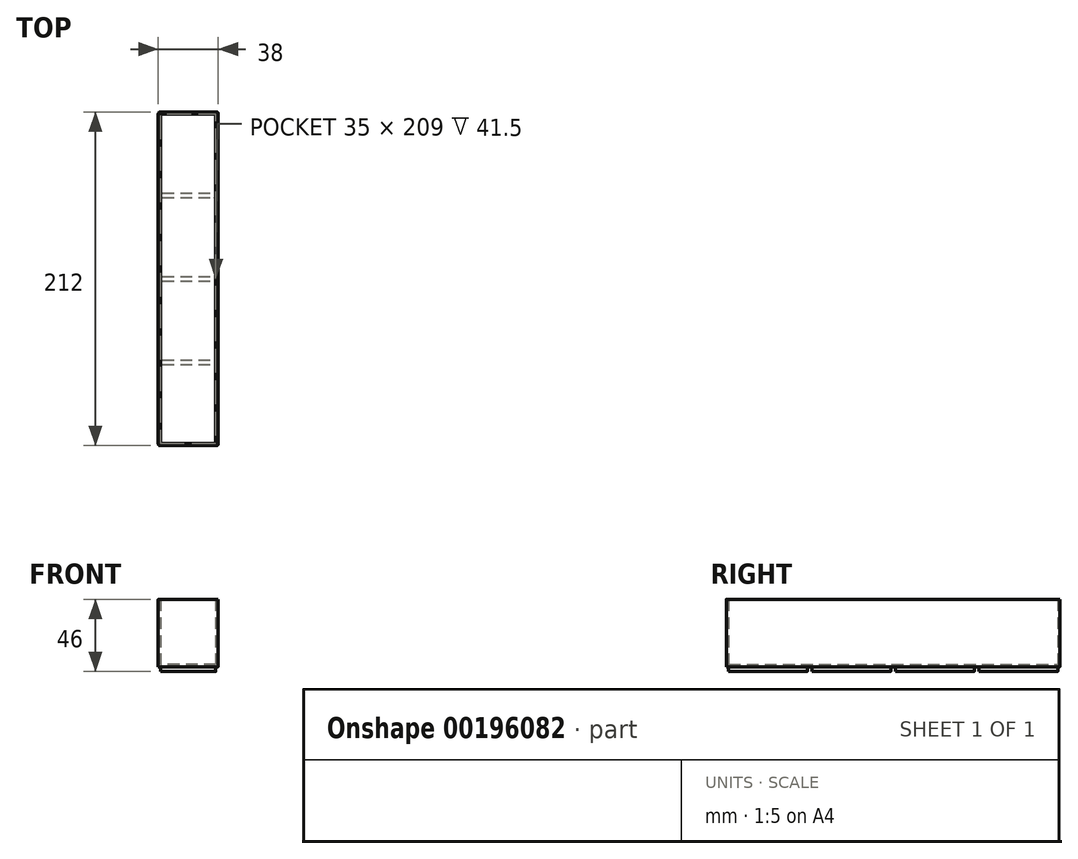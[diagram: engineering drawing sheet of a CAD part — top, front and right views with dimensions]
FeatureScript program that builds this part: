
annotation { "Feature Type Name" : "Feature", "Feature Type Description" : "" }
export const myFeature = defineFeature(function(context is Context, id is Id, definition is map)
    precondition{}
    {
        {
            var Q0;
            Q0=qCreatedBy(makeId("Top.planeOp"),FACE);
            var sketch = newSketch(context, id + "F0", { "sketchPlane" : qUnion([Q0])});
            skLineSegment(sketch, "E0.bottom", {"start": v(0, 0) * mm, "end": v(38, 0) * mm});
            skLineSegment(sketch, "E0.top", {"start": v(0, 53) * mm, "end": v(38, 53) * mm});
            skLineSegment(sketch, "E0.left", {"start": v(0, 0) * mm, "end": v(0, 53) * mm});
            skLineSegment(sketch, "E0.right", {"start": v(38, 0) * mm, "end": v(38, 53) * mm});
            skLineSegment(sketch, "E1.bottom", {"start": v(1.5, 1.5) * mm, "end": v(36.5, 1.5) * mm});
            skLineSegment(sketch, "E1.top", {"start": v(1.5, 51.5) * mm, "end": v(36.5, 51.5) * mm});
            skLineSegment(sketch, "E1.left", {"start": v(1.5, 1.5) * mm, "end": v(1.5, 51.5) * mm});
            skLineSegment(sketch, "E1.right", {"start": v(36.5, 1.5) * mm, "end": v(36.5, 51.5) * mm});
            skLineSegment(sketch, "E2.top", {"start": v(0, 106) * mm, "end": v(38, 106) * mm});
            skLineSegment(sketch, "E2.left", {"start": v(0, 53) * mm, "end": v(0, 106) * mm});
            skLineSegment(sketch, "E2.right", {"start": v(38, 53) * mm, "end": v(38, 106) * mm});
            skLineSegment(sketch, "E3.bottom", {"start": v(1.5, 54.5) * mm, "end": v(36.5, 54.5) * mm});
            skLineSegment(sketch, "E3.top", {"start": v(1.5, 104.5) * mm, "end": v(36.5, 104.5) * mm});
            skLineSegment(sketch, "E3.left", {"start": v(1.5, 54.5) * mm, "end": v(1.5, 104.5) * mm});
            skLineSegment(sketch, "E3.right", {"start": v(36.5, 54.5) * mm, "end": v(36.5, 104.5) * mm});
            skLineSegment(sketch, "E4.top", {"start": v(0, 159) * mm, "end": v(38, 159) * mm});
            skLineSegment(sketch, "E4.left", {"start": v(0, 106) * mm, "end": v(0, 159) * mm});
            skLineSegment(sketch, "E4.right", {"start": v(38, 106) * mm, "end": v(38, 159) * mm});
            skLineSegment(sketch, "E5.bottom", {"start": v(38, 159) * mm, "end": v(0, 159) * mm});
            skLineSegment(sketch, "E5.top", {"start": v(38, 212) * mm, "end": v(0, 212) * mm});
            skLineSegment(sketch, "E5.left", {"start": v(38, 159) * mm, "end": v(38, 212) * mm});
            skLineSegment(sketch, "E5.right", {"start": v(0, 159) * mm, "end": v(0, 212) * mm});
            skLineSegment(sketch, "E6.bottom", {"start": v(1.5, 107.5) * mm, "end": v(36.5, 107.5) * mm});
            skLineSegment(sketch, "E6.top", {"start": v(1.5, 157.5) * mm, "end": v(36.5, 157.5) * mm});
            skLineSegment(sketch, "E6.left", {"start": v(1.5, 107.5) * mm, "end": v(1.5, 157.5) * mm});
            skLineSegment(sketch, "E6.right", {"start": v(36.5, 107.5) * mm, "end": v(36.5, 157.5) * mm});
            skLineSegment(sketch, "E7.bottom", {"start": v(1.5, 160.5) * mm, "end": v(36.5, 160.5) * mm});
            skLineSegment(sketch, "E7.top", {"start": v(1.5, 210.5) * mm, "end": v(36.5, 210.5) * mm});
            skLineSegment(sketch, "E7.left", {"start": v(1.5, 160.5) * mm, "end": v(1.5, 210.5) * mm});
            skLineSegment(sketch, "E7.right", {"start": v(36.5, 160.5) * mm, "end": v(36.5, 210.5) * mm});
            skLineSegment(sketch, "E8", {"start": v(1.5, 160.5) * mm, "end": v(1.5, 157.5) * mm});
            skLineSegment(sketch, "E9", {"start": v(36.5, 160.5) * mm, "end": v(36.5, 157.5) * mm});
            skLineSegment(sketch, "E10", {"start": v(1.5, 107.5) * mm, "end": v(1.5, 104.5) * mm});
            skLineSegment(sketch, "E11", {"start": v(36.5, 107.5) * mm, "end": v(36.5, 104.5) * mm});
            skLineSegment(sketch, "E12", {"start": v(36.5, 54.5) * mm, "end": v(36.5, 51.5) * mm});
            skLineSegment(sketch, "E13", {"start": v(1.5, 54.5) * mm, "end": v(1.5, 51.5) * mm});
            skSolve(sketch);
        }
        {
            var Q0;
            Q0=makeQuery(id+"F0.imprint","IMPRINT",FACE,{"disambiguationData":[TD([[makeQuery(id+"F0.imprint","IMPRINT",EDGE,{"derivedFrom":sQuery(id+"F0.wireOp",EDGE,"E7.bottom")}),1.0]])]});
            var Q1;
            Q1=makeQuery(id+"F0.imprint","IMPRINT",FACE,{"disambiguationData":[TD([[makeQuery(id+"F0.imprint","IMPRINT",EDGE,{"derivedFrom":sQuery(id+"F0.wireOp",EDGE,"E6.bottom")}),1.0]])]});
            var Q2;
            Q2=makeQuery(id+"F0.imprint","IMPRINT",FACE,{"disambiguationData":[TD([[makeQuery(id+"F0.imprint","IMPRINT",EDGE,{"derivedFrom":sQuery(id+"F0.wireOp",EDGE,"E3.bottom")}),1.0]])]});
            var Q3;
            Q3=makeQuery(id+"F0.imprint","IMPRINT",FACE,{"disambiguationData":[TD([[makeQuery(id+"F0.imprint","IMPRINT",EDGE,{"derivedFrom":sQuery(id+"F0.wireOp",EDGE,"E1.bottom")}),1.0]])]});
            extrude(context, id + "F1", {"entities" : qUnion([Q0, Q1, Q2, Q3]), "oppositeDirection" : true, "depth" : 3 * mm, "offsetDistance" : 25 * mm});
        }
        {
            var Q0;
            Q0=makeQuery(id+"F0.imprint","IMPRINT",FACE,{"disambiguationData":[TD([[makeQuery(id+"F0.imprint","IMPRINT",EDGE,{"derivedFrom":sQuery(id+"F0.wireOp",EDGE,"E7.bottom")}),1.0]])]});
            var Q1;
            Q1=makeQuery(id+"F0.imprint","IMPRINT",FACE,{"disambiguationData":[TD([[makeQuery(id+"F0.imprint","IMPRINT",EDGE,{"derivedFrom":sQuery(id+"F0.wireOp",EDGE,"E5.top")}),1.0]])]});
            var Q2;
            Q2=makeQuery(id+"F0.imprint","IMPRINT",FACE,{"disambiguationData":[TD([[makeQuery(id+"F0.imprint","IMPRINT",EDGE,{"derivedFrom":sQuery(id+"F0.wireOp",EDGE,"E6.bottom")}),1.0]])]});
            var Q3;
            {var subQ1=sQuery(id+"F0.wireOp",EDGE,"E4.right");Q3=makeQuery(id+"F0.imprint","IMPRINT",FACE,{"disambiguationData":[TD([[makeQuery(id+"F0.imprint","IMPRINT",EDGE,{"derivedFrom":subQ1}),1.0]])]});}
            var Q4;
            {var subQ5=sQuery(id+"F0.wireOp",EDGE,"E6.top");Q4=makeQuery(id+"F0.imprint","IMPRINT",FACE,{"disambiguationData":[TD([[makeQuery(id+"F0.imprint","IMPRINT",EDGE,{"derivedFrom":subQ5}),1.0]])]});}
            var Q5;
            {var subQ5=sQuery(id+"F0.wireOp",EDGE,"E7.bottom");Q5=makeQuery(id+"F0.imprint","IMPRINT",FACE,{"disambiguationData":[TD([[makeQuery(id+"F0.imprint","IMPRINT",EDGE,{"derivedFrom":subQ5}),-1.0]])]});}
            var Q6;
            {var subQ1=sQuery(id+"F0.wireOp",EDGE,"E4.left");Q6=makeQuery(id+"F0.imprint","IMPRINT",FACE,{"disambiguationData":[TD([[makeQuery(id+"F0.imprint","IMPRINT",EDGE,{"derivedFrom":subQ1}),-1.0]])]});}
            var Q7;
            {var subQ0=sQuery(id+"F0.wireOp",EDGE,"E3.top");Q7=makeQuery(id+"F0.imprint","IMPRINT",FACE,{"disambiguationData":[TD([[makeQuery(id+"F0.imprint","IMPRINT",EDGE,{"derivedFrom":subQ0}),1.0]])]});}
            var Q8;
            {var subQ5=sQuery(id+"F0.wireOp",EDGE,"E6.bottom");Q8=makeQuery(id+"F0.imprint","IMPRINT",FACE,{"disambiguationData":[TD([[makeQuery(id+"F0.imprint","IMPRINT",EDGE,{"derivedFrom":subQ5}),-1.0]])]});}
            var Q9;
            {var subQ1=sQuery(id+"F0.wireOp",EDGE,"E2.right");Q9=makeQuery(id+"F0.imprint","IMPRINT",FACE,{"disambiguationData":[TD([[makeQuery(id+"F0.imprint","IMPRINT",EDGE,{"derivedFrom":subQ1}),1.0]])]});}
            var Q10;
            Q10=makeQuery(id+"F0.imprint","IMPRINT",FACE,{"disambiguationData":[TD([[makeQuery(id+"F0.imprint","IMPRINT",EDGE,{"derivedFrom":sQuery(id+"F0.wireOp",EDGE,"E3.bottom")}),1.0]])]});
            var Q11;
            {var subQ1=sQuery(id+"F0.wireOp",EDGE,"E2.left");Q11=makeQuery(id+"F0.imprint","IMPRINT",FACE,{"disambiguationData":[TD([[makeQuery(id+"F0.imprint","IMPRINT",EDGE,{"derivedFrom":subQ1}),-1.0]])]});}
            var Q12;
            Q12=makeQuery(id+"F0.imprint","IMPRINT",FACE,{"disambiguationData":[TD([[makeQuery(id+"F0.imprint","IMPRINT",EDGE,{"derivedFrom":sQuery(id+"F0.wireOp",EDGE,"E0.bottom")}),1.0]])]});
            var Q13;
            Q13=makeQuery(id+"F0.imprint","IMPRINT",FACE,{"disambiguationData":[TD([[makeQuery(id+"F0.imprint","IMPRINT",EDGE,{"derivedFrom":sQuery(id+"F0.wireOp",EDGE,"E1.bottom")}),1.0]])]});
            var Q14;
            {var subQ0=sQuery(id+"F0.wireOp",EDGE,"E1.top");Q14=makeQuery(id+"F0.imprint","IMPRINT",FACE,{"disambiguationData":[TD([[makeQuery(id+"F0.imprint","IMPRINT",EDGE,{"derivedFrom":subQ0}),1.0]])]});}
            var Q15;
            {var subQ5=sQuery(id+"F0.wireOp",EDGE,"E3.bottom");Q15=makeQuery(id+"F0.imprint","IMPRINT",FACE,{"disambiguationData":[TD([[makeQuery(id+"F0.imprint","IMPRINT",EDGE,{"derivedFrom":subQ5}),-1.0]])]});}
            extrude(context, id + "F2", {"entities" : qUnion([Q0, Q1, Q2, Q3, Q4, Q5, Q6, Q7, Q8, Q9, Q10, Q11, Q12, Q13, Q14, Q15]), "operationType" : NewBodyOperationType.ADD, "depth" : 1.5 * mm, "offsetDistance" : 25 * mm});
        }
        {
            var Q0;
            Q0=makeQuery(id+"F0.imprint","IMPRINT",FACE,{"disambiguationData":[TD([[makeQuery(id+"F0.imprint","IMPRINT",EDGE,{"derivedFrom":sQuery(id+"F0.wireOp",EDGE,"E0.bottom")}),1.0]])]});
            var Q1;
            {var subQ1=sQuery(id+"F0.wireOp",EDGE,"E2.left");Q1=makeQuery(id+"F0.imprint","IMPRINT",FACE,{"disambiguationData":[TD([[makeQuery(id+"F0.imprint","IMPRINT",EDGE,{"derivedFrom":subQ1}),-1.0]])]});}
            var Q2;
            {var subQ1=sQuery(id+"F0.wireOp",EDGE,"E2.right");Q2=makeQuery(id+"F0.imprint","IMPRINT",FACE,{"disambiguationData":[TD([[makeQuery(id+"F0.imprint","IMPRINT",EDGE,{"derivedFrom":subQ1}),1.0]])]});}
            var Q3;
            {var subQ1=sQuery(id+"F0.wireOp",EDGE,"E4.right");Q3=makeQuery(id+"F0.imprint","IMPRINT",FACE,{"disambiguationData":[TD([[makeQuery(id+"F0.imprint","IMPRINT",EDGE,{"derivedFrom":subQ1}),1.0]])]});}
            var Q4;
            {var subQ1=sQuery(id+"F0.wireOp",EDGE,"E4.left");Q4=makeQuery(id+"F0.imprint","IMPRINT",FACE,{"disambiguationData":[TD([[makeQuery(id+"F0.imprint","IMPRINT",EDGE,{"derivedFrom":subQ1}),-1.0]])]});}
            var Q5;
            Q5=makeQuery(id+"F0.imprint","IMPRINT",FACE,{"disambiguationData":[TD([[makeQuery(id+"F0.imprint","IMPRINT",EDGE,{"derivedFrom":sQuery(id+"F0.wireOp",EDGE,"E5.top")}),1.0]])]});
            extrude(context, id + "F3", {"entities" : qUnion([Q0, Q1, Q2, Q3, Q4, Q5]), "operationType" : NewBodyOperationType.ADD, "depth" : 43 * mm, "offsetDistance" : 25 * mm});
        }
        {
            var Q0;
            {var subQ0=sQuery(id+"F0.wireOp",EDGE,"E5.left");var subQ1=sQuery(id+"F0.wireOp",EDGE,"E5.top");Q0=makeQuery(id+"F3.boolean.opBoolean","MERGE",EDGE,{"derivedFrom":[makeQuery(id+"F2.opExtrude","SWEPT_EDGE",EDGE,{"disambiguationData":[OSD([subQ1,subQ0])]}),makeQuery(id+"F3.opExtrude","SWEPT_EDGE",EDGE,{"disambiguationData":[OSD([subQ1,subQ0])]})]});}
            var Q1;
            {var subQ0=sQuery(id+"F0.wireOp",EDGE,"E5.right");var subQ1=sQuery(id+"F0.wireOp",EDGE,"E5.top");Q1=makeQuery(id+"F3.boolean.opBoolean","MERGE",EDGE,{"derivedFrom":[makeQuery(id+"F2.opExtrude","SWEPT_EDGE",EDGE,{"disambiguationData":[OSD([subQ1,subQ0])]}),makeQuery(id+"F3.opExtrude","SWEPT_EDGE",EDGE,{"disambiguationData":[OSD([subQ1,subQ0])]})]});}
            var Q2;
            Q2=makeQuery(id+"F1.opExtrude","SWEPT_EDGE",EDGE,{"disambiguationData":[OSD([sQuery(id+"F0.wireOp",EDGE,"E7.top"),sQuery(id+"F0.wireOp",EDGE,"E7.left")])]});
            var Q3;
            Q3=makeQuery(id+"F1.opExtrude","SWEPT_EDGE",EDGE,{"disambiguationData":[OSD([sQuery(id+"F0.wireOp",EDGE,"E7.top"),sQuery(id+"F0.wireOp",EDGE,"E7.right")])]});
            var Q4;
            Q4=makeQuery(id+"F1.opExtrude","SWEPT_EDGE",EDGE,{"disambiguationData":[OSD([sQuery(id+"F0.wireOp",EDGE,"E7.bottom"),sQuery(id+"F0.wireOp",EDGE,"E7.left"),sQuery(id+"F0.wireOp",EDGE,"E8")])]});
            var Q5;
            Q5=makeQuery(id+"F1.opExtrude","SWEPT_EDGE",EDGE,{"disambiguationData":[OSD([sQuery(id+"F0.wireOp",EDGE,"E7.bottom"),sQuery(id+"F0.wireOp",EDGE,"E7.right"),sQuery(id+"F0.wireOp",EDGE,"E9")])]});
            var Q6;
            Q6=makeQuery(id+"F1.opExtrude","SWEPT_EDGE",EDGE,{"disambiguationData":[OSD([sQuery(id+"F0.wireOp",EDGE,"E6.top"),sQuery(id+"F0.wireOp",EDGE,"E6.right"),sQuery(id+"F0.wireOp",EDGE,"E9")])]});
            var Q7;
            Q7=makeQuery(id+"F1.opExtrude","SWEPT_EDGE",EDGE,{"disambiguationData":[OSD([sQuery(id+"F0.wireOp",EDGE,"E6.top"),sQuery(id+"F0.wireOp",EDGE,"E6.left"),sQuery(id+"F0.wireOp",EDGE,"E8")])]});
            var Q8;
            Q8=makeQuery(id+"F1.opExtrude","SWEPT_EDGE",EDGE,{"disambiguationData":[OSD([sQuery(id+"F0.wireOp",EDGE,"E6.bottom"),sQuery(id+"F0.wireOp",EDGE,"E6.left"),sQuery(id+"F0.wireOp",EDGE,"E10")])]});
            var Q9;
            Q9=makeQuery(id+"F1.opExtrude","SWEPT_EDGE",EDGE,{"disambiguationData":[OSD([sQuery(id+"F0.wireOp",EDGE,"E6.bottom"),sQuery(id+"F0.wireOp",EDGE,"E6.right"),sQuery(id+"F0.wireOp",EDGE,"E11")])]});
            var Q10;
            Q10=makeQuery(id+"F1.opExtrude","SWEPT_EDGE",EDGE,{"disambiguationData":[OSD([sQuery(id+"F0.wireOp",EDGE,"E3.top"),sQuery(id+"F0.wireOp",EDGE,"E3.right"),sQuery(id+"F0.wireOp",EDGE,"E11")])]});
            var Q11;
            Q11=makeQuery(id+"F1.opExtrude","SWEPT_EDGE",EDGE,{"disambiguationData":[OSD([sQuery(id+"F0.wireOp",EDGE,"E3.top"),sQuery(id+"F0.wireOp",EDGE,"E3.left"),sQuery(id+"F0.wireOp",EDGE,"E10")])]});
            var Q12;
            Q12=makeQuery(id+"F1.opExtrude","SWEPT_EDGE",EDGE,{"disambiguationData":[OSD([sQuery(id+"F0.wireOp",EDGE,"E3.bottom"),sQuery(id+"F0.wireOp",EDGE,"E3.left"),sQuery(id+"F0.wireOp",EDGE,"E13")])]});
            var Q13;
            Q13=makeQuery(id+"F1.opExtrude","SWEPT_EDGE",EDGE,{"disambiguationData":[OSD([sQuery(id+"F0.wireOp",EDGE,"E3.bottom"),sQuery(id+"F0.wireOp",EDGE,"E3.right"),sQuery(id+"F0.wireOp",EDGE,"E12")])]});
            var Q14;
            Q14=makeQuery(id+"F1.opExtrude","SWEPT_EDGE",EDGE,{"disambiguationData":[OSD([sQuery(id+"F0.wireOp",EDGE,"E1.top"),sQuery(id+"F0.wireOp",EDGE,"E1.right"),sQuery(id+"F0.wireOp",EDGE,"E12")])]});
            var Q15;
            Q15=makeQuery(id+"F1.opExtrude","SWEPT_EDGE",EDGE,{"disambiguationData":[OSD([sQuery(id+"F0.wireOp",EDGE,"E1.top"),sQuery(id+"F0.wireOp",EDGE,"E1.left"),sQuery(id+"F0.wireOp",EDGE,"E13")])]});
            var Q16;
            Q16=makeQuery(id+"F1.opExtrude","SWEPT_EDGE",EDGE,{"disambiguationData":[OSD([sQuery(id+"F0.wireOp",EDGE,"E1.bottom"),sQuery(id+"F0.wireOp",EDGE,"E1.left")])]});
            var Q17;
            Q17=makeQuery(id+"F1.opExtrude","SWEPT_EDGE",EDGE,{"disambiguationData":[OSD([sQuery(id+"F0.wireOp",EDGE,"E1.bottom"),sQuery(id+"F0.wireOp",EDGE,"E1.right")])]});
            var Q18;
            {var subQ0=sQuery(id+"F0.wireOp",EDGE,"E0.right");var subQ1=sQuery(id+"F0.wireOp",EDGE,"E0.bottom");Q18=makeQuery(id+"F3.boolean.opBoolean","MERGE",EDGE,{"derivedFrom":[makeQuery(id+"F2.opExtrude","SWEPT_EDGE",EDGE,{"disambiguationData":[OSD([subQ1,subQ0])]}),makeQuery(id+"F3.opExtrude","SWEPT_EDGE",EDGE,{"disambiguationData":[OSD([subQ1,subQ0])]})]});}
            var Q19;
            {var subQ0=sQuery(id+"F0.wireOp",EDGE,"E0.left");var subQ1=sQuery(id+"F0.wireOp",EDGE,"E0.bottom");Q19=makeQuery(id+"F3.boolean.opBoolean","MERGE",EDGE,{"derivedFrom":[makeQuery(id+"F2.opExtrude","SWEPT_EDGE",EDGE,{"disambiguationData":[OSD([subQ1,subQ0])]}),makeQuery(id+"F3.opExtrude","SWEPT_EDGE",EDGE,{"disambiguationData":[OSD([subQ1,subQ0])]})]});}
            fillet(context, id + "F4", {"entities" : qUnion([Q0, Q1, Q2, Q3, Q4, Q5, Q6, Q7, Q8, Q9, Q10, Q11, Q12, Q13, Q14, Q15, Q16, Q17, Q18, Q19]), "radius" : 1 * mm, "tangentPropagation" : true, "allowEdgeOverflow" : false});
        }
    });
